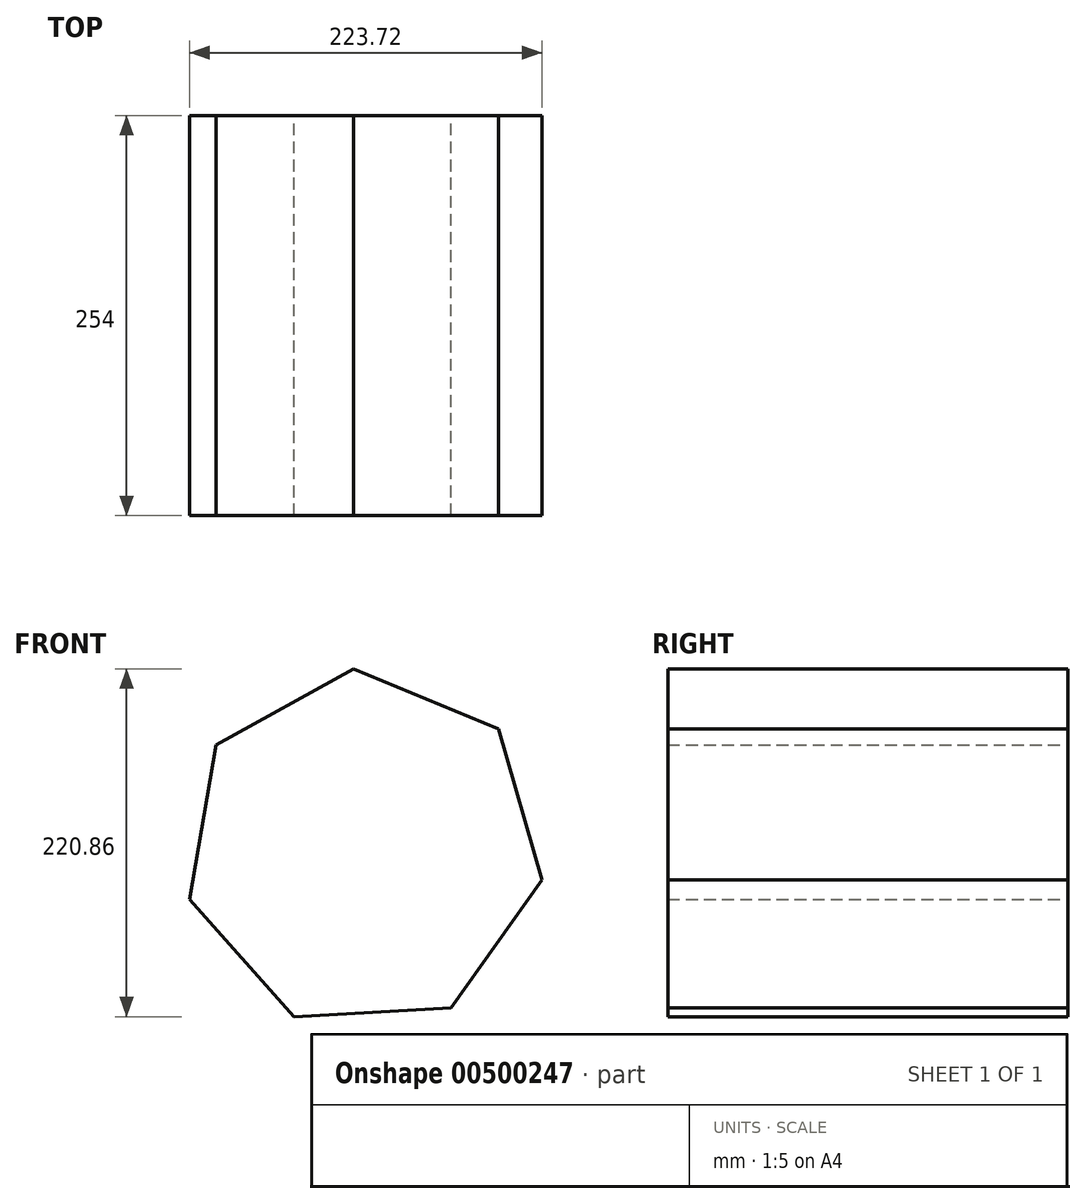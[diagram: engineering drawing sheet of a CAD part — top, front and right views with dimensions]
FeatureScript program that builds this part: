
annotation { "Feature Type Name" : "Feature", "Feature Type Description" : "" }
export const myFeature = defineFeature(function(context is Context, id is Id, definition is map)
    precondition{}
    {
        {
            var Q0;
            Q0=qCreatedBy(makeId("Front.planeOp"),FACE);
            var sketch = newSketch(context, id + "F0", { "sketchPlane" : qUnion([Q0])});
            skCircle(sketch, "E0.cCircle", {"center": v(0, 0) * mm, "radius": 114.91 * mm, "construction": true});
            skLineSegment(sketch, "E0.0", {"start": v(-110.45, -31.7) * mm, "end": v(-93.65, 66.59) * mm});
            skLineSegment(sketch, "E0.1", {"start": v(-93.65, 66.59) * mm, "end": v(-6.33, 114.74) * mm});
            skLineSegment(sketch, "E0.2", {"start": v(-6.33, 114.74) * mm, "end": v(85.76, 76.48) * mm});
            skLineSegment(sketch, "E0.3", {"start": v(85.76, 76.48) * mm, "end": v(113.27, -19.36) * mm});
            skLineSegment(sketch, "E0.4", {"start": v(113.27, -19.36) * mm, "end": v(55.48, -100.63) * mm});
            skLineSegment(sketch, "E0.5", {"start": v(55.48, -100.63) * mm, "end": v(-44.08, -106.12) * mm});
            skLineSegment(sketch, "E0.6", {"start": v(-44.08, -106.12) * mm, "end": v(-110.45, -31.7) * mm});
            skSolve(sketch);
        }
        {
            var Q0;
            Q0=makeQuery(id+"F0.imprint","IMPRINT",FACE,{"disambiguationData":[TD([[makeQuery(id+"F0.imprint","IMPRINT",EDGE,{"derivedFrom":sQuery(id+"F0.wireOp",EDGE,"E0.0")}),-1.0]])]});
            extrude(context, id + "F1", {"entities" : qUnion([Q0]), "depth" : 254 * mm, "offsetDistance" : 25 * mm});
        }
    });
